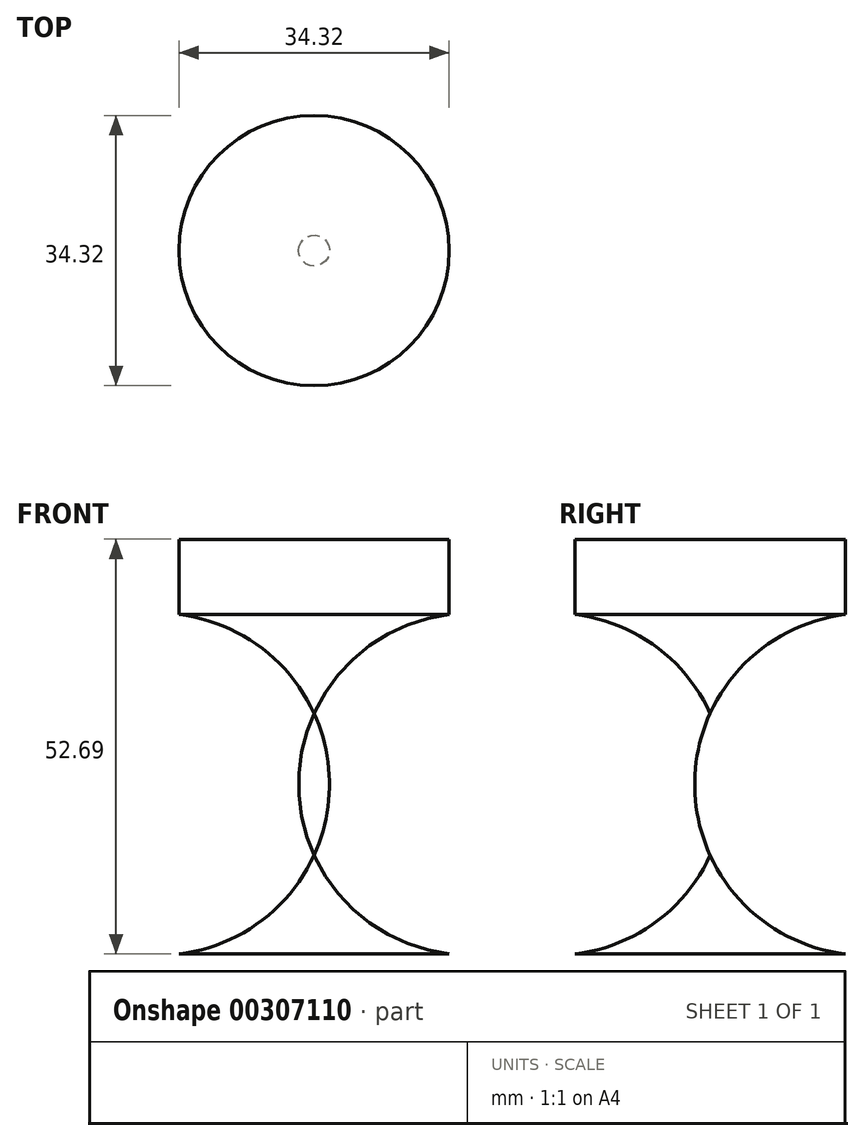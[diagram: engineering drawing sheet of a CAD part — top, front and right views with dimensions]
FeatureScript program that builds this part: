
annotation { "Feature Type Name" : "Feature", "Feature Type Description" : "" }
export const myFeature = defineFeature(function(context is Context, id is Id, definition is map)
    precondition{}
    {
        {
            var Q0;
            Q0=qCreatedBy(makeId("Front.planeOp"),FACE);
            var sketch = newSketch(context, id + "F0", { "sketchPlane" : qUnion([Q0])});
            skLineSegment(sketch, "E0", {"start": v(0, 77.42) * mm, "end": v(0, -78) * mm});
            skSolve(sketch);
        }
        {
            var Q0;
            Q0=qCreatedBy(makeId("Front.planeOp"),FACE);
            var sketch = newSketch(context, id + "F1", { "sketchPlane" : qUnion([Q0])});
            skLineSegment(sketch, "E1", {"start": v(0, 0) * mm, "end": v(17.16, 0) * mm});
            skArc(sketch, "E2", {"start": v(17.16, 0) * mm, "mid": v(41.45, 21.55) * mm, "end": v(17.16, 43.1) * mm});
            skLineSegment(sketch, "E3", {"start": v(17.16, 43.1) * mm, "end": v(17.16, 52.69) * mm});
            skLineSegment(sketch, "E4", {"start": v(17.16, 52.69) * mm, "end": v(0, 52.69) * mm});
            skLineSegment(sketch, "E5", {"start": v(0, 52.69) * mm, "end": v(0, 0) * mm});
            skSolve(sketch);
        }
        {
            var Q0;
            Q0=makeQuery(id+"F1.imprint","IMPRINT",FACE,{"disambiguationData":[TD([[makeQuery(id+"F1.imprint","IMPRINT",EDGE,{"derivedFrom":sQuery(id+"F1.wireOp",EDGE,"E1")}),1.0]])]});
            var Q1;
            Q1=sQuery(id+"F0.wireOp",EDGE,"E0");
            revolve(context, id + "F2", {"entities" : qUnion([Q0]), "axis" : qUnion([Q1]), "revolveType" : RevolveType.FULL});
        }
        {
            var Q0;
            Q0=qCreatedBy(makeId("Front.planeOp"),FACE);
            var sketch = newSketch(context, id + "F3", { "sketchPlane" : qUnion([Q0])});
            skLineSegment(sketch, "E6", {"start": v(-17.02, 23.78) * mm, "end": v(-6.16, 23.78) * mm});
            skLineSegment(sketch, "E7", {"start": v(-6.16, 23.78) * mm, "end": v(-9.4, 32.3) * mm});
            skLineSegment(sketch, "E8", {"start": v(-9.4, 32.3) * mm, "end": v(-17.02, 23.78) * mm});
            skLineSegment(sketch, "E9", {"start": v(15.56, 23.78) * mm, "end": v(27.3, 23.78) * mm});
            skLineSegment(sketch, "E10", {"start": v(27.3, 23.78) * mm, "end": v(19.37, 35.23) * mm});
            skLineSegment(sketch, "E11", {"start": v(19.37, 35.23) * mm, "end": v(15.56, 23.78) * mm});
            skLineSegment(sketch, "E12", {"start": v(-6.16, 13.8) * mm, "end": v(15.56, 13.8) * mm});
            skLineSegment(sketch, "E13", {"start": v(15.56, 13.8) * mm, "end": v(10.86, 5.29) * mm});
            skLineSegment(sketch, "E14", {"start": v(10.86, 5.29) * mm, "end": v(0, 5.29) * mm});
            skLineSegment(sketch, "E15", {"start": v(0, 5.29) * mm, "end": v(-6.16, 13.8) * mm});
            skSolve(sketch);
        }
        {
            var Q0;
            Q0 = qSketchRegion(id + "F3", true);
            extrude(context, id + "F4", {"entities" : qUnion([Q0]), "operationType" : NewBodyOperationType.REMOVE, "endBound" : BoundingType.SYMMETRIC, "oppositeDirection" : true, "depth" : 127 * mm});
        }
    });
